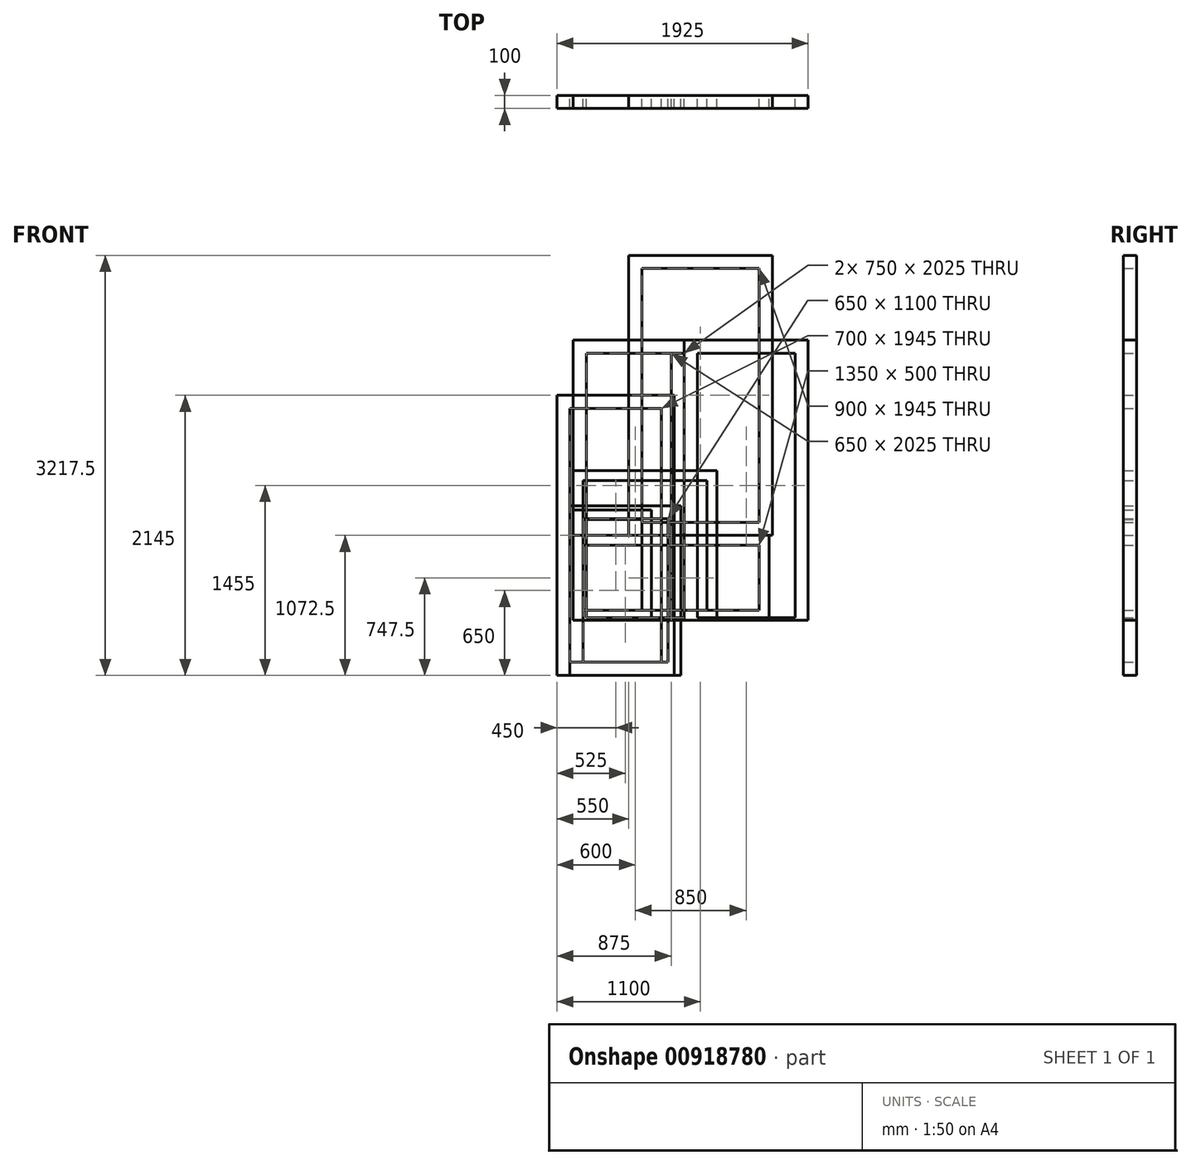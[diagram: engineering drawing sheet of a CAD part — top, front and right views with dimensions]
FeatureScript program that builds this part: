
annotation { "Feature Type Name" : "Feature", "Feature Type Description" : "" }
export const myFeature = defineFeature(function(context is Context, id is Id, definition is map)
    precondition{}
    {
        {
            var Q0;
            Q0=qCreatedBy(makeId("Front.planeOp"),FACE);
            var sketch = newSketch(context, id + "F0", { "sketchPlane" : qUnion([Q0])});
            skLineSegment(sketch, "E0.bottom", {"start": v(0, 0) * mm, "end": v(1100, 0) * mm});
            skLineSegment(sketch, "E0.top", {"start": v(0, 2145) * mm, "end": v(1100, 2145) * mm});
            skLineSegment(sketch, "E0.left", {"start": v(0, 0) * mm, "end": v(0, 2145) * mm});
            skLineSegment(sketch, "E0.right", {"start": v(1100, 0) * mm, "end": v(1100, 2145) * mm});
            skLineSegment(sketch, "E1.0", {"start": v(100, 100) * mm, "end": v(100, 2045) * mm});
            skLineSegment(sketch, "E1.1", {"start": v(100, 100) * mm, "end": v(1000, 100) * mm});
            skLineSegment(sketch, "E1.2", {"start": v(1000, 100) * mm, "end": v(1000, 2045) * mm});
            skLineSegment(sketch, "E1.3", {"start": v(100, 2045) * mm, "end": v(1000, 2045) * mm});
            skSolve(sketch);
        }
        {
            var Q0;
            Q0=makeQuery(id+"F0.imprint","IMPRINT",FACE,{"disambiguationData":[TD([[makeQuery(id+"F0.imprint","IMPRINT",EDGE,{"derivedFrom":sQuery(id+"F0.wireOp",EDGE,"E0.bottom")}),1.0]])]});
            extrude(context, id + "F1", {"entities" : qUnion([Q0]), "depth" : 100 * mm, "offsetDistance" : 25 * mm});
        }
        {
            var Q0;
            Q0=qCreatedBy(makeId("Front.planeOp"),FACE);
            var sketch = newSketch(context, id + "F2", { "sketchPlane" : qUnion([Q0])});
            skLineSegment(sketch, "E2.bottom", {"start": v(-550, -1072.5) * mm, "end": v(350, -1072.5) * mm});
            skLineSegment(sketch, "E2.top", {"start": v(-550, 1072.5) * mm, "end": v(350, 1072.5) * mm});
            skLineSegment(sketch, "E2.left", {"start": v(-550, -1072.5) * mm, "end": v(-550, 1072.5) * mm});
            skLineSegment(sketch, "E2.right", {"start": v(350, -1072.5) * mm, "end": v(350, 1072.5) * mm});
            skLineSegment(sketch, "E3.0", {"start": v(-450, -972.5) * mm, "end": v(-450, 972.5) * mm});
            skLineSegment(sketch, "E3.1", {"start": v(-450, -972.5) * mm, "end": v(250, -972.5) * mm});
            skLineSegment(sketch, "E3.2", {"start": v(250, -972.5) * mm, "end": v(250, 972.5) * mm});
            skLineSegment(sketch, "E3.3", {"start": v(-450, 972.5) * mm, "end": v(250, 972.5) * mm});
            skSolve(sketch);
        }
        {
            var Q0;
            Q0=makeQuery(id+"F2.imprint","IMPRINT",FACE,{"disambiguationData":[TD([[makeQuery(id+"F2.imprint","IMPRINT",EDGE,{"derivedFrom":sQuery(id+"F2.wireOp",EDGE,"E2.bottom")}),1.0]])]});
            extrude(context, id + "F3", {"entities" : qUnion([Q0]), "depth" : 100 * mm, "offsetDistance" : 25 * mm});
        }
        {
            var Q0;
            Q0=qCreatedBy(makeId("Front.planeOp"),FACE);
            var sketch = newSketch(context, id + "F4", { "sketchPlane" : qUnion([Q0])});
            skLineSegment(sketch, "E4.bottom", {"start": v(-450, -1072.5) * mm, "end": v(400, -1072.5) * mm});
            skLineSegment(sketch, "E4.top", {"start": v(-450, 227.5) * mm, "end": v(400, 227.5) * mm});
            skLineSegment(sketch, "E4.left", {"start": v(-450, -1072.5) * mm, "end": v(-450, 227.5) * mm});
            skLineSegment(sketch, "E4.right", {"start": v(400, -1072.5) * mm, "end": v(400, 227.5) * mm});
            skLineSegment(sketch, "E5.0", {"start": v(-350, -972.5) * mm, "end": v(-350, 127.5) * mm});
            skLineSegment(sketch, "E5.1", {"start": v(-350, -972.5) * mm, "end": v(300, -972.5) * mm});
            skLineSegment(sketch, "E5.2", {"start": v(300, -972.5) * mm, "end": v(300, 127.5) * mm});
            skLineSegment(sketch, "E5.3", {"start": v(-350, 127.5) * mm, "end": v(300, 127.5) * mm});
            skSolve(sketch);
        }
        {
            var Q0;
            Q0=makeQuery(id+"F4.imprint","IMPRINT",FACE,{"disambiguationData":[TD([[makeQuery(id+"F4.imprint","IMPRINT",EDGE,{"derivedFrom":sQuery(id+"F4.wireOp",EDGE,"E4.bottom")}),1.0]])]});
            extrude(context, id + "F5", {"entities" : qUnion([Q0]), "depth" : 100 * mm, "offsetDistance" : 25 * mm});
        }
        {
            var Q0;
            Q0=qCreatedBy(makeId("Front.planeOp"),FACE);
            var sketch = newSketch(context, id + "F6", { "sketchPlane" : qUnion([Q0])});
            skLineSegment(sketch, "E6.bottom", {"start": v(-425, -650) * mm, "end": v(475, -650) * mm});
            skLineSegment(sketch, "E6.top", {"start": v(-425, 1495) * mm, "end": v(475, 1495) * mm});
            skLineSegment(sketch, "E6.left", {"start": v(-425, -650) * mm, "end": v(-425, 1495) * mm});
            skLineSegment(sketch, "E6.right", {"start": v(475, -650) * mm, "end": v(475, 1495) * mm});
            skLineSegment(sketch, "E7.0", {"start": v(-325, -630) * mm, "end": v(-325, 1395) * mm});
            skLineSegment(sketch, "E7.1", {"start": v(-325, -630) * mm, "end": v(425, -630) * mm});
            skLineSegment(sketch, "E7.2", {"start": v(425, -630) * mm, "end": v(425, 1395) * mm});
            skLineSegment(sketch, "E7.3", {"start": v(-325, 1395) * mm, "end": v(425, 1395) * mm});
            skLineSegment(sketch, "E8.bottom", {"start": v(475, -650) * mm, "end": v(1375, -650) * mm});
            skLineSegment(sketch, "E8.top", {"start": v(475, 1495) * mm, "end": v(1375, 1495) * mm});
            skLineSegment(sketch, "E8.right", {"start": v(1375, -650) * mm, "end": v(1375, 1495) * mm});
            skLineSegment(sketch, "E9.bottom", {"start": v(525, 1395) * mm, "end": v(1275, 1395) * mm});
            skLineSegment(sketch, "E9.top", {"start": v(525, -630) * mm, "end": v(1275, -630) * mm});
            skLineSegment(sketch, "E9.left", {"start": v(525, 1395) * mm, "end": v(525, -630) * mm});
            skLineSegment(sketch, "E9.right", {"start": v(1275, 1395) * mm, "end": v(1275, -630) * mm});
            skSolve(sketch);
        }
        {
            var Q0;
            Q0=makeQuery(id+"F6.imprint","IMPRINT",FACE,{"disambiguationData":[TD([[makeQuery(id+"F6.imprint","IMPRINT",EDGE,{"derivedFrom":sQuery(id+"F6.wireOp",EDGE,"E6.bottom")}),1.0]])]});
            var Q1;
            Q1=makeQuery(id+"F6.imprint","IMPRINT",FACE,{"disambiguationData":[TD([[makeQuery(id+"F6.imprint","IMPRINT",EDGE,{"derivedFrom":sQuery(id+"F6.wireOp",EDGE,"E8.bottom")}),1.0]])]});
            extrude(context, id + "F7", {"entities" : qUnion([Q0, Q1]), "depth" : 100 * mm, "offsetDistance" : 25 * mm});
        }
        {
            var Q0;
            Q0=qCreatedBy(makeId("Front.planeOp"),FACE);
            var sketch = newSketch(context, id + "F8", { "sketchPlane" : qUnion([Q0])});
            skLineSegment(sketch, "E10.bottom", {"start": v(-425, -650) * mm, "end": v(425, -650) * mm});
            skLineSegment(sketch, "E10.top", {"start": v(-425, 1495) * mm, "end": v(425, 1495) * mm});
            skLineSegment(sketch, "E10.left", {"start": v(-425, -650) * mm, "end": v(-425, 1495) * mm});
            skLineSegment(sketch, "E10.right", {"start": v(425, -650) * mm, "end": v(425, 1495) * mm});
            skLineSegment(sketch, "E11.0", {"start": v(-325, -630) * mm, "end": v(-325, 1395) * mm});
            skLineSegment(sketch, "E11.1", {"start": v(-325, -630) * mm, "end": v(325, -630) * mm});
            skLineSegment(sketch, "E11.2", {"start": v(325, -630) * mm, "end": v(325, 1395) * mm});
            skLineSegment(sketch, "E11.3", {"start": v(-325, 1395) * mm, "end": v(325, 1395) * mm});
            skSolve(sketch);
        }
        {
            var Q0;
            Q0=makeQuery(id+"F8.imprint","IMPRINT",FACE,{"disambiguationData":[TD([[makeQuery(id+"F8.imprint","IMPRINT",EDGE,{"derivedFrom":sQuery(id+"F8.wireOp",EDGE,"E10.bottom")}),1.0]])]});
            extrude(context, id + "F9", {"entities" : qUnion([Q0]), "depth" : 100 * mm, "offsetDistance" : 25 * mm});
        }
        {
            var Q0;
            Q0=qCreatedBy(makeId("Front.planeOp"),FACE);
            var sketch = newSketch(context, id + "F10", { "sketchPlane" : qUnion([Q0])});
            skLineSegment(sketch, "E12.bottom", {"start": v(-425, -650) * mm, "end": v(1075, -650) * mm});
            skLineSegment(sketch, "E12.top", {"start": v(-425, 0) * mm, "end": v(1075, 0) * mm});
            skLineSegment(sketch, "E12.left", {"start": v(-425, -650) * mm, "end": v(-425, 0) * mm});
            skLineSegment(sketch, "E12.right", {"start": v(1075, -650) * mm, "end": v(1075, 0) * mm});
            skLineSegment(sketch, "E13.0", {"start": v(-350, -575) * mm, "end": v(-350, -75) * mm});
            skLineSegment(sketch, "E13.1", {"start": v(-350, -575) * mm, "end": v(1000, -575) * mm});
            skLineSegment(sketch, "E13.2", {"start": v(1000, -575) * mm, "end": v(1000, -75) * mm});
            skLineSegment(sketch, "E13.3", {"start": v(-350, -75) * mm, "end": v(1000, -75) * mm});
            skSolve(sketch);
        }
        {
            var Q0;
            Q0=makeQuery(id+"F10.imprint","IMPRINT",FACE,{"disambiguationData":[TD([[makeQuery(id+"F10.imprint","IMPRINT",EDGE,{"derivedFrom":sQuery(id+"F10.wireOp",EDGE,"E12.bottom")}),1.0]])]});
            extrude(context, id + "F11", {"entities" : qUnion([Q0]), "depth" : 100 * mm, "offsetDistance" : 25 * mm});
        }
        {
            var Q0;
            Q0=qCreatedBy(makeId("Front.planeOp"),FACE);
            var sketch = newSketch(context, id + "F12", { "sketchPlane" : qUnion([Q0])});
            skLineSegment(sketch, "E14.bottom", {"start": v(-425, -650) * mm, "end": v(175, -650) * mm});
            skLineSegment(sketch, "E14.top", {"start": v(-425, 195) * mm, "end": v(175, 195) * mm});
            skLineSegment(sketch, "E14.left", {"start": v(-425, -650) * mm, "end": v(-425, 195) * mm});
            skLineSegment(sketch, "E14.right", {"start": v(175, -650) * mm, "end": v(175, 195) * mm});
            skLineSegment(sketch, "E15.0", {"start": v(-350, -575) * mm, "end": v(-350, 120) * mm});
            skLineSegment(sketch, "E15.1", {"start": v(-350, -575) * mm, "end": v(100, -575) * mm});
            skLineSegment(sketch, "E15.2", {"start": v(100, -575) * mm, "end": v(100, 120) * mm});
            skLineSegment(sketch, "E15.3", {"start": v(-350, 120) * mm, "end": v(100, 120) * mm});
            skSolve(sketch);
        }
        {
            var Q0;
            Q0=makeQuery(id+"F12.imprint","IMPRINT",FACE,{"disambiguationData":[TD([[makeQuery(id+"F12.imprint","IMPRINT",EDGE,{"derivedFrom":sQuery(id+"F12.wireOp",EDGE,"E14.bottom")}),1.0]])]});
            extrude(context, id + "F13", {"entities" : qUnion([Q0]), "depth" : 100 * mm, "offsetDistance" : 25 * mm});
        }
        {
            var Q0;
            Q0=qCreatedBy(makeId("Front.planeOp"),FACE);
            var sketch = newSketch(context, id + "F14", { "sketchPlane" : qUnion([Q0])});
            skLineSegment(sketch, "E16.bottom", {"start": v(-425, -650) * mm, "end": v(675, -650) * mm});
            skLineSegment(sketch, "E16.top", {"start": v(-425, 495) * mm, "end": v(675, 495) * mm});
            skLineSegment(sketch, "E16.left", {"start": v(-425, -650) * mm, "end": v(-425, 495) * mm});
            skLineSegment(sketch, "E16.right", {"start": v(675, -650) * mm, "end": v(675, 495) * mm});
            skLineSegment(sketch, "E17.0", {"start": v(-350, -575) * mm, "end": v(-350, 420) * mm});
            skLineSegment(sketch, "E17.1", {"start": v(-350, -575) * mm, "end": v(600, -575) * mm});
            skLineSegment(sketch, "E17.2", {"start": v(600, -575) * mm, "end": v(600, 420) * mm});
            skLineSegment(sketch, "E17.3", {"start": v(-350, 420) * mm, "end": v(600, 420) * mm});
            skSolve(sketch);
        }
        {
            var Q0;
            Q0=makeQuery(id+"F14.imprint","IMPRINT",FACE,{"disambiguationData":[TD([[makeQuery(id+"F14.imprint","IMPRINT",EDGE,{"derivedFrom":sQuery(id+"F14.wireOp",EDGE,"E16.bottom")}),1.0]])]});
            extrude(context, id + "F15", {"entities" : qUnion([Q0]), "depth" : 100 * mm, "offsetDistance" : 25 * mm});
        }
    });
